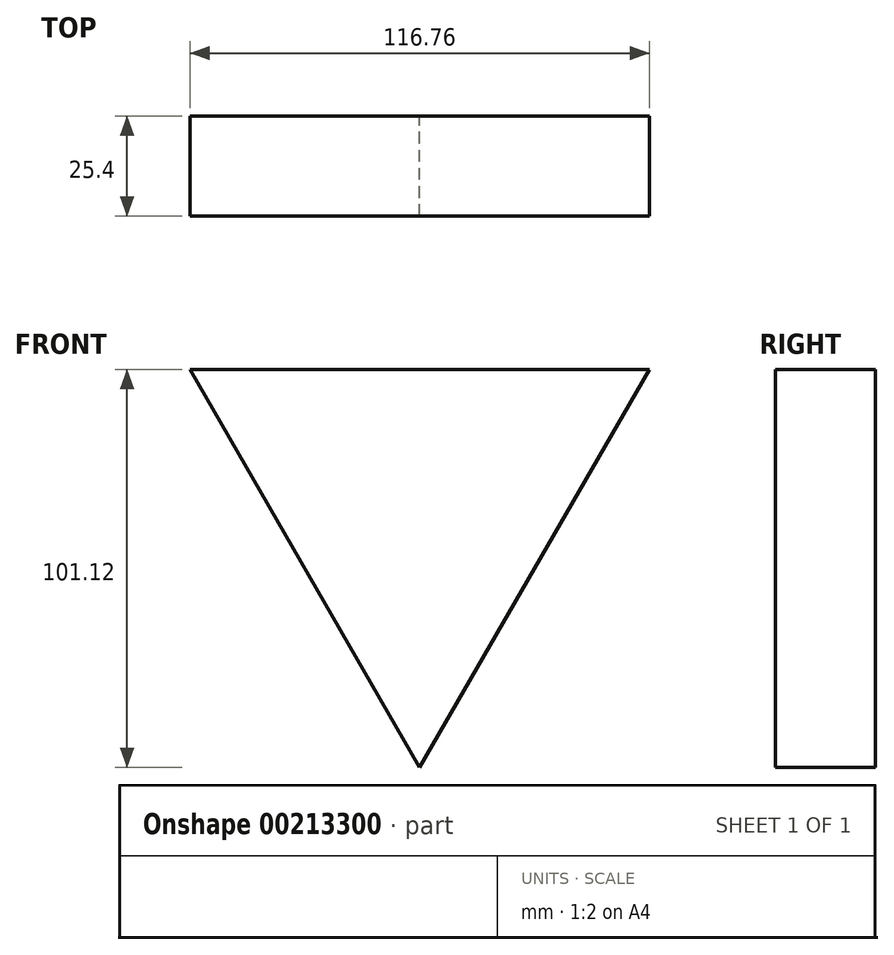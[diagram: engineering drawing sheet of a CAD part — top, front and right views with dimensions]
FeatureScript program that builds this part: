
annotation { "Feature Type Name" : "Feature", "Feature Type Description" : "" }
export const myFeature = defineFeature(function(context is Context, id is Id, definition is map)
    precondition{}
    {
        {
            var Q0;
            Q0=qCreatedBy(makeId("Front.planeOp"),FACE);
            var sketch = newSketch(context, id + "F0", { "sketchPlane" : qUnion([Q0])});
            skCircle(sketch, "E0.cCircle", {"center": v(0, 0) * mm, "radius": 67.41 * mm, "construction": true});
            skLineSegment(sketch, "E0.0", {"start": v(0, -67.41) * mm, "end": v(-58.38, 33.7) * mm});
            skLineSegment(sketch, "E0.1", {"start": v(-58.38, 33.7) * mm, "end": v(58.38, 33.7) * mm});
            skLineSegment(sketch, "E0.2", {"start": v(58.38, 33.7) * mm, "end": v(0, -67.41) * mm});
            skSolve(sketch);
        }
        {
            var Q0;
            Q0=makeQuery(id+"F0.imprint","IMPRINT",FACE,{"disambiguationData":[TD([[makeQuery(id+"F0.imprint","IMPRINT",EDGE,{"derivedFrom":sQuery(id+"F0.wireOp",EDGE,"E0.0")}),-1.0]])]});
            extrude(context, id + "F1", {"entities" : qUnion([Q0]), "depth" : 25.4 * mm});
        }
        {
            var Q0;
            Q0=qCreatedBy(makeId("Front.planeOp"),FACE);
            var sketch = newSketch(context, id + "F2", { "sketchPlane" : qUnion([Q0])});
            skCircle(sketch, "E1", {"center": v(0, 0) * mm, "radius": 70.57 * mm});
            skSolve(sketch);
        }
        {
            var Q0;
            Q0=sQuery(id+"F2.wireOp",EDGE,"E1");
            extrude(context, id + "F3", {"bodyType" : ToolBodyType.SURFACE, "surfaceEntities" : qUnion([Q0]), "depth" : 25.4 * mm});
        }
    });
